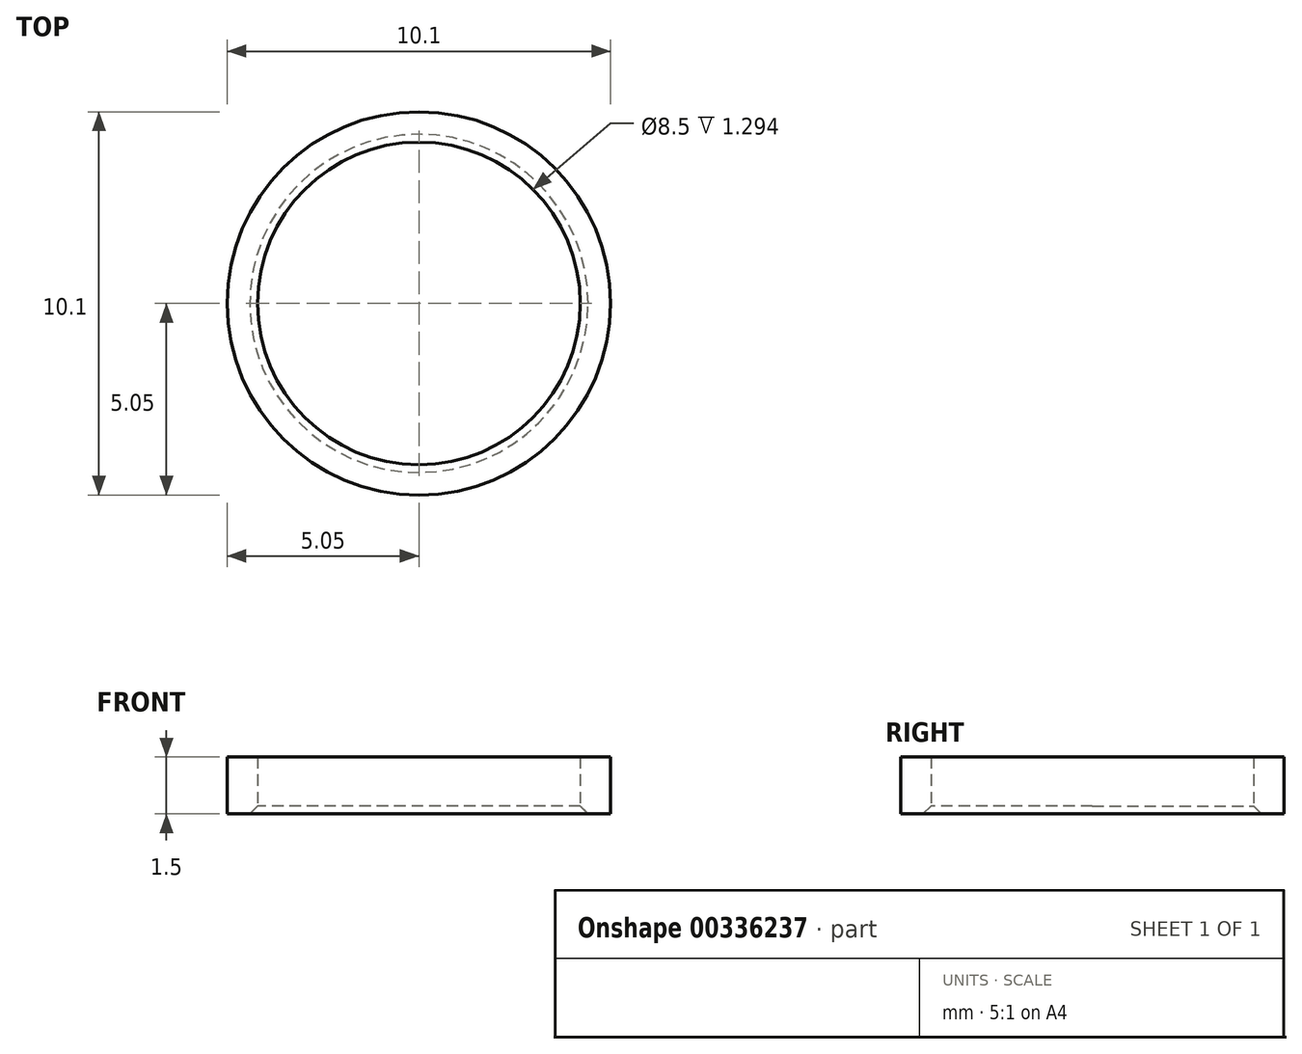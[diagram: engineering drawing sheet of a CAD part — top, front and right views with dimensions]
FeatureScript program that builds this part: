
annotation { "Feature Type Name" : "Feature", "Feature Type Description" : "" }
export const myFeature = defineFeature(function(context is Context, id is Id, definition is map)
    precondition{}
    {
        {
            var Q0;
            Q0=qCreatedBy(makeId("Front.planeOp"),FACE);
            var sketch = newSketch(context, id + "F0", { "sketchPlane" : qUnion([Q0])});
            skLineSegment(sketch, "E0.bottom", {"start": v(-5.05, 0) * mm, "end": v(-4.25, 0) * mm});
            skLineSegment(sketch, "E0.top", {"start": v(-5.05, 1.5) * mm, "end": v(-4.25, 1.5) * mm});
            skLineSegment(sketch, "E0.left", {"start": v(-5.05, 0) * mm, "end": v(-5.05, 1.5) * mm});
            skLineSegment(sketch, "E0.right", {"start": v(-4.25, 0) * mm, "end": v(-4.25, 1.5) * mm});
            skLineSegment(sketch, "E1", {"start": v(0, 0) * mm, "end": v(0, 5.04) * mm, "construction": true});
            skSolve(sketch);
        }
        {
            var Q0;
            Q0 = qSketchRegion(id + "F0", true);
            var Q1;
            Q1=sQuery(id+"F0.wireOp",EDGE,"E1");
            revolve(context, id + "F1", {"entities" : qUnion([Q0]), "axis" : qUnion([Q1]), "revolveType" : RevolveType.FULL});
        }
        {
            var Q0;
            Q0=makeQuery(id+"F1.opRevolve","SWEPT_EDGE",EDGE,{"disambiguationData":[OSD([sQuery(id+"F0.wireOp",EDGE,"E0.bottom"),sQuery(id+"F0.wireOp",EDGE,"E0.right")])]});
            chamfer(context, id + "F2", {"entities" : qUnion([Q0]), "width" : 0.2 * mm});
        }
    });
